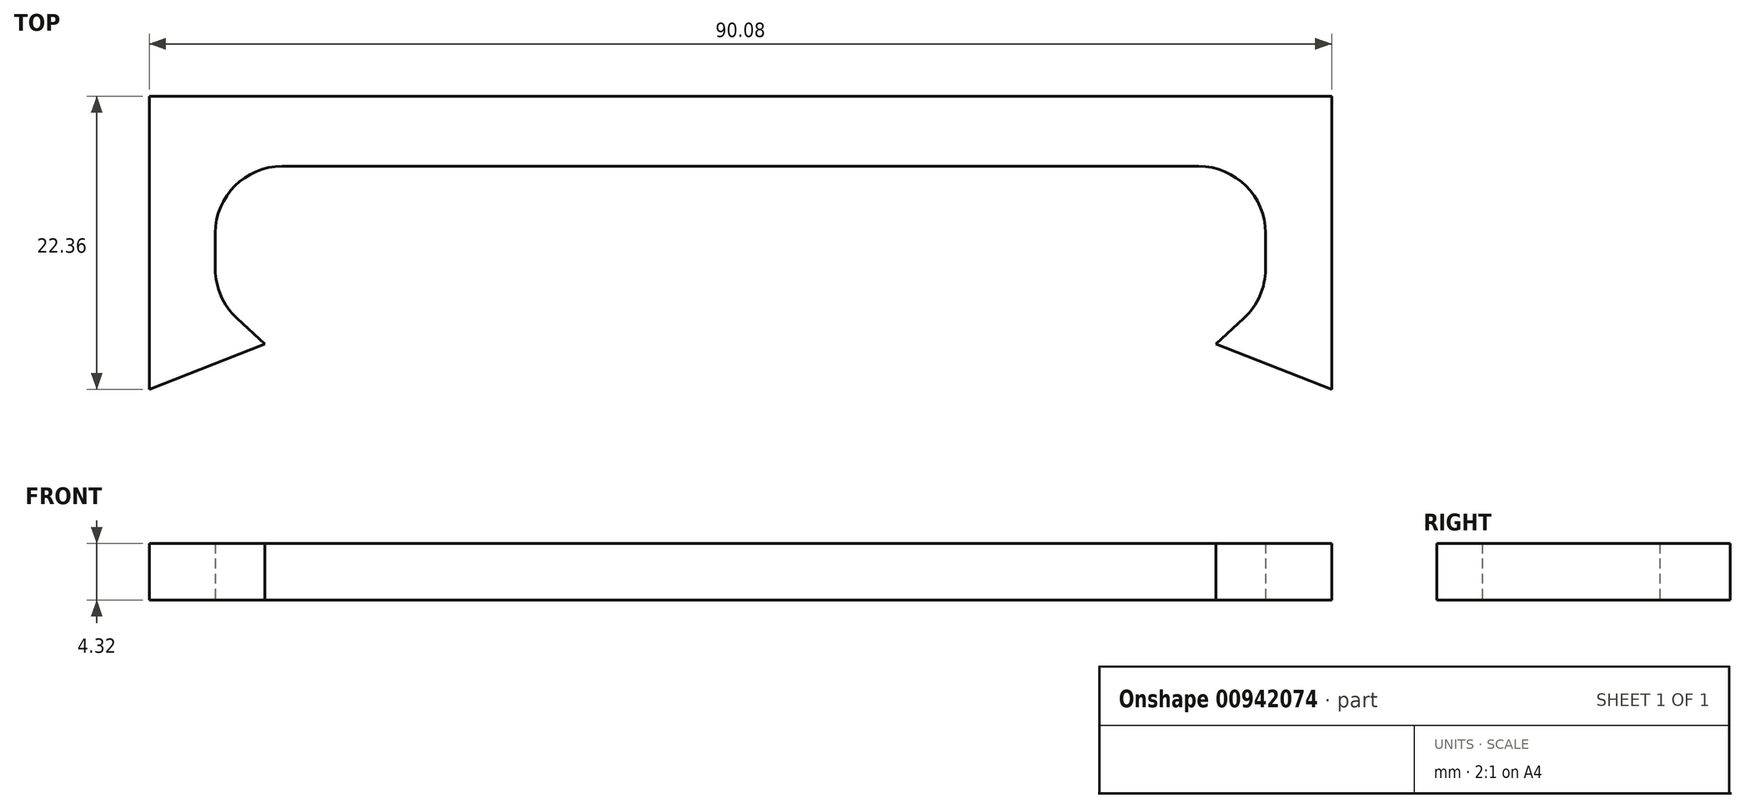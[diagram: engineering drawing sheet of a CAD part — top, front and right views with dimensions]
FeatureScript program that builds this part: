
annotation { "Feature Type Name" : "Feature", "Feature Type Description" : "" }
export const myFeature = defineFeature(function(context is Context, id is Id, definition is map)
    precondition{}
    {
        {
            var Q0;
            Q0=qCreatedBy(makeId("Top.planeOp"),FACE);
            var sketch = newSketch(context, id + "F0", { "sketchPlane" : qUnion([Q0])});
            skLineSegment(sketch, "E0", {"start": v(-36.68, -5.39) * mm, "end": v(-32.9, -8.85) * mm});
            skLineSegment(sketch, "E1", {"start": v(-32.9, -8.85) * mm, "end": v(-41.72, -12.32) * mm});
            skLineSegment(sketch, "E2", {"start": v(-41.72, -12.32) * mm, "end": v(-41.72, 10.04) * mm});
            skLineSegment(sketch, "E3", {"start": v(-41.72, 10.04) * mm, "end": v(48.36, 10.04) * mm});
            skLineSegment(sketch, "E4", {"start": v(48.36, 10.04) * mm, "end": v(48.36, -12.32) * mm});
            skLineSegment(sketch, "E5", {"start": v(48.36, -12.32) * mm, "end": v(39.54, -8.85) * mm});
            skLineSegment(sketch, "E6", {"start": v(39.54, -8.85) * mm, "end": v(43.32, -5.39) * mm});
            skLineSegment(sketch, "E7", {"start": v(43.32, -5.39) * mm, "end": v(43.32, 4.69) * mm});
            skLineSegment(sketch, "E8", {"start": v(43.32, 4.69) * mm, "end": v(-36.68, 4.69) * mm});
            skLineSegment(sketch, "E9", {"start": v(-36.68, 4.69) * mm, "end": v(-36.68, -5.39) * mm});
            skSolve(sketch);
        }
        {
            var Q0;
            Q0 = qSketchRegion(id + "F0", true);
            extrude(context, id + "F1", {"entities" : qUnion([Q0]), "depth" : 4.32 * mm, "offsetDistance" : 25.4 * mm});
        }
        {
            var Q0;
            Q0=makeQuery(id+"F1.opExtrude","SWEPT_EDGE",EDGE,{"disambiguationData":[OSD([sQuery(id+"F0.wireOp",EDGE,"E8"),sQuery(id+"F0.wireOp",EDGE,"E9")])]});
            var Q1;
            Q1=makeQuery(id+"F1.opExtrude","SWEPT_EDGE",EDGE,{"disambiguationData":[OSD([sQuery(id+"F0.wireOp",EDGE,"E7"),sQuery(id+"F0.wireOp",EDGE,"E8")])]});
            var Q2;
            Q2=makeQuery(id+"F1.opExtrude","SWEPT_EDGE",EDGE,{"disambiguationData":[OSD([sQuery(id+"F0.wireOp",EDGE,"E0"),sQuery(id+"F0.wireOp",EDGE,"E9")])]});
            var Q3;
            Q3=makeQuery(id+"F1.opExtrude","SWEPT_EDGE",EDGE,{"disambiguationData":[OSD([sQuery(id+"F0.wireOp",EDGE,"E6"),sQuery(id+"F0.wireOp",EDGE,"E7")])]});
            fillet(context, id + "F2", {"entities" : qUnion([Q0, Q1, Q2, Q3]), "radius" : 5.08 * mm, "tangentPropagation" : true, "allowEdgeOverflow" : false});
        }
    });
